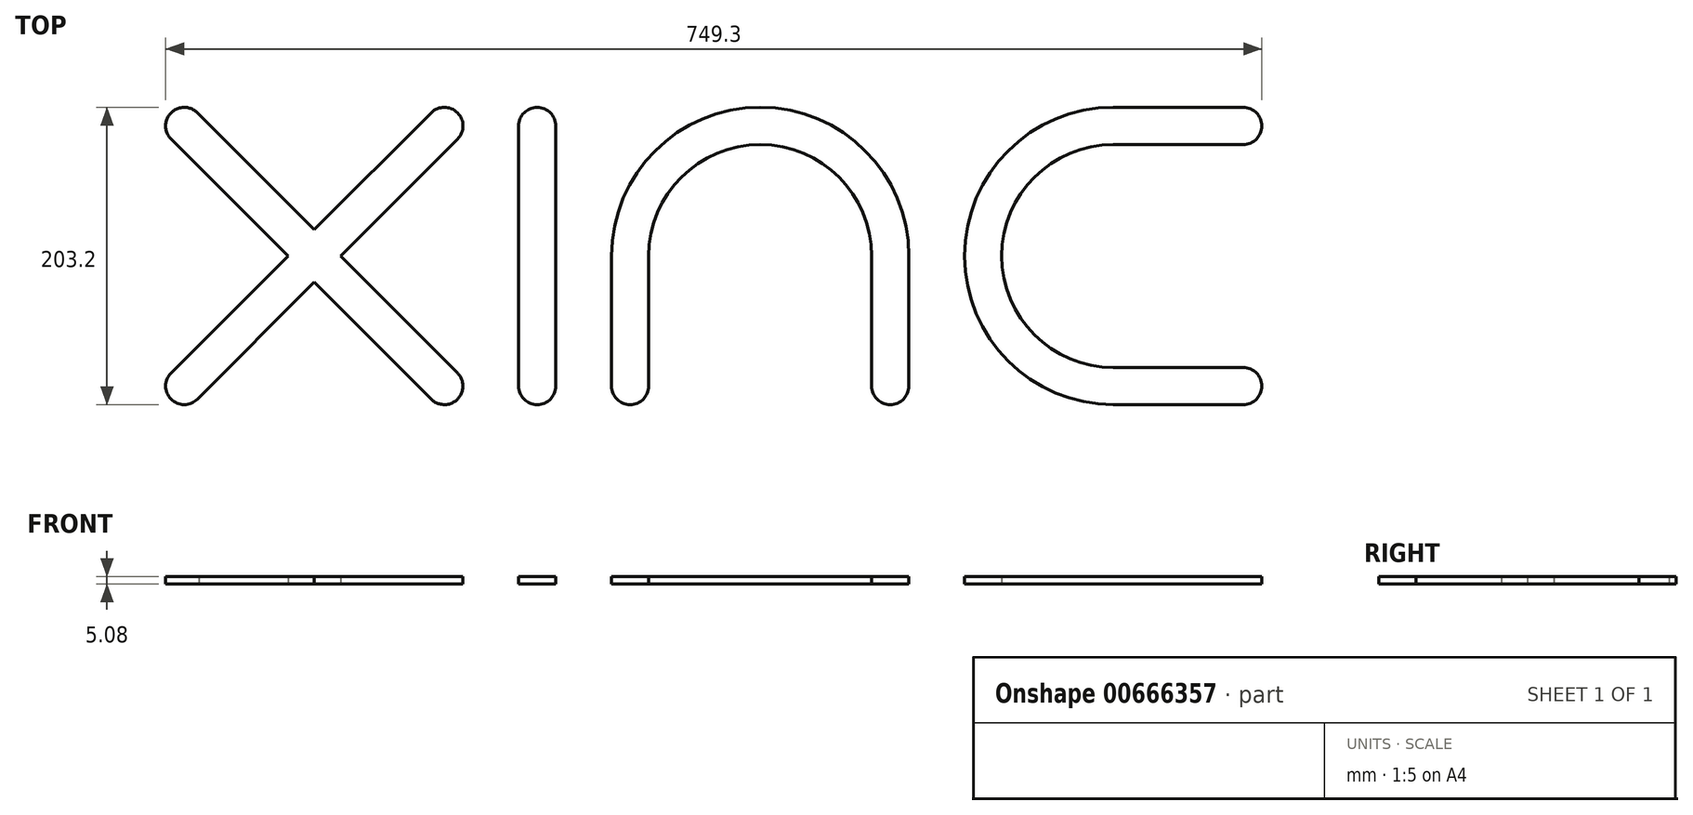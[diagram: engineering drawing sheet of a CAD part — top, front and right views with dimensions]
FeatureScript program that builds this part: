
annotation { "Feature Type Name" : "Feature", "Feature Type Description" : "" }
export const myFeature = defineFeature(function(context is Context, id is Id, definition is map)
    precondition{}
    {
        {
            var Q0;
            Q0=qCreatedBy(makeId("Top.planeOp"),FACE);
            var sketch = newSketch(context, id + "F0", { "sketchPlane" : qUnion([Q0])});
            skArc(sketch, "E0", {"start": v(-282.12, 96.75) * mm, "mid": v(-300.53, 98.4) * mm, "end": v(-301.08, 79.92) * mm});
            skArc(sketch, "E1", {"start": v(-123.28, -97.88) * mm, "mid": v(-105.32, -97.88) * mm, "end": v(-105.32, -79.92) * mm});
            skArc(sketch, "E2", {"start": v(-105.32, 79.92) * mm, "mid": v(-105.32, 97.88) * mm, "end": v(-123.28, 97.88) * mm});
            skArc(sketch, "E3", {"start": v(-301.08, -79.92) * mm, "mid": v(-301.08, -97.88) * mm, "end": v(-283.12, -97.88) * mm});
            skLineSegment(sketch, "E4", {"start": v(-301.08, 79.92) * mm, "end": v(-221.16, 0) * mm});
            skLineSegment(sketch, "E5", {"start": v(-282.12, 96.75) * mm, "end": v(-203.24, 17.93) * mm});
            skLineSegment(sketch, "E6", {"start": v(-123.28, 97.88) * mm, "end": v(-203.24, 17.93) * mm});
            skLineSegment(sketch, "E7", {"start": v(-283.12, -97.88) * mm, "end": v(-203.2, -17.96) * mm});
            skLineSegment(sketch, "E8", {"start": v(-292.1, -88.9) * mm, "end": v(-114.3, 88.9) * mm, "construction": true});
            skLineSegment(sketch, "E9", {"start": v(-292.1, 88.9) * mm, "end": v(-114.3, -88.9) * mm, "construction": true});
            skPoint(sketch, "E10", {"position": v(-203.2, 0) * mm});
            skLineSegment(sketch, "E11.trimOffspring", {"start": v(-221.16, 0) * mm, "end": v(-301.08, -79.92) * mm});
            skLineSegment(sketch, "E12.trimOffspring", {"start": v(-203.2, -17.96) * mm, "end": v(-123.28, -97.88) * mm});
            skLineSegment(sketch, "E13.trimOffspring", {"start": v(-185.27, -0.03) * mm, "end": v(-105.32, -79.92) * mm});
            skLineSegment(sketch, "E14.trimOffspring", {"start": v(-185.27, -0.03) * mm, "end": v(-105.32, 79.92) * mm});
            skArc(sketch, "E15", {"start": v(-38.1, 88.9) * mm, "mid": v(-50.8, 101.6) * mm, "end": v(-63.5, 88.9) * mm});
            skArc(sketch, "E16", {"start": v(-63.5, -88.9) * mm, "mid": v(-50.8, -101.6) * mm, "end": v(-38.1, -88.9) * mm});
            skLineSegment(sketch, "E17", {"start": v(-63.5, 88.9) * mm, "end": v(-63.5, -88.9) * mm});
            skLineSegment(sketch, "E18", {"start": v(-38.1, 88.9) * mm, "end": v(-38.1, -88.9) * mm});
            skLineSegment(sketch, "E19", {"start": v(-292.1, 88.9) * mm, "end": v(469.7, 88.9) * mm, "construction": true});
            skLineSegment(sketch, "E20", {"start": v(-292.1, -88.9) * mm, "end": v(469.7, -88.9) * mm, "construction": true});
            skArc(sketch, "E21", {"start": v(0, -88.9) * mm, "mid": v(12.7, -101.6) * mm, "end": v(25.4, -88.9) * mm});
            skArc(sketch, "E22", {"start": v(177.8, -88.9) * mm, "mid": v(190.5, -101.6) * mm, "end": v(203.2, -88.9) * mm});
            skPoint(sketch, "E23.center.orphan", {"position": v(12.7, 88.9) * mm});
            skLineSegment(sketch, "E24", {"start": v(0, -88.9) * mm, "end": v(0, 0) * mm});
            skArc(sketch, "E25", {"start": v(177.8, 0) * mm, "mid": v(101.6, 76.2) * mm, "end": v(25.4, 0) * mm});
            skLineSegment(sketch, "E26", {"start": v(25.4, -88.9) * mm, "end": v(25.4, 0) * mm});
            skLineSegment(sketch, "E27", {"start": v(203.2, 0) * mm, "end": v(203.2, -88.9) * mm});
            skLineSegment(sketch, "E28", {"start": v(177.8, -88.9) * mm, "end": v(177.8, 0) * mm});
            skArc(sketch, "E29.trimOffspring", {"start": v(203.2, 0) * mm, "mid": v(101.6, 101.6) * mm, "end": v(0, 0) * mm});
            skArc(sketch, "E30", {"start": v(342.9, 76.2) * mm, "mid": v(266.7, 0) * mm, "end": v(342.9, -76.2) * mm});
            skArc(sketch, "E31", {"start": v(431.8, 76.2) * mm, "mid": v(444.5, 88.9) * mm, "end": v(431.8, 101.6) * mm});
            skArc(sketch, "E32", {"start": v(431.8, -101.6) * mm, "mid": v(444.5, -88.9) * mm, "end": v(431.8, -76.2) * mm});
            skLineSegment(sketch, "E33", {"start": v(431.8, 76.2) * mm, "end": v(342.9, 76.2) * mm});
            skLineSegment(sketch, "E34", {"start": v(431.8, 101.6) * mm, "end": v(342.9, 101.6) * mm});
            skLineSegment(sketch, "E35", {"start": v(431.8, -101.6) * mm, "end": v(342.9, -101.6) * mm});
            skLineSegment(sketch, "E36", {"start": v(431.8, -76.2) * mm, "end": v(342.9, -76.2) * mm});
            skArc(sketch, "E37.trimOffspring", {"start": v(342.9, 101.6) * mm, "mid": v(241.3, 0) * mm, "end": v(342.9, -101.6) * mm});
            skCircle(sketch, "E38", {"center": v(254, 0) * mm, "radius": 12.7 * mm, "construction": true});
            skSolve(sketch);
        }
        {
            var Q0;
            Q0 = qSketchRegion(id + "F0", true);
            extrude(context, id + "F1", {"entities" : qUnion([Q0]), "depth" : 5.08 * mm, "offsetDistance" : 25.4 * mm});
        }
    });
